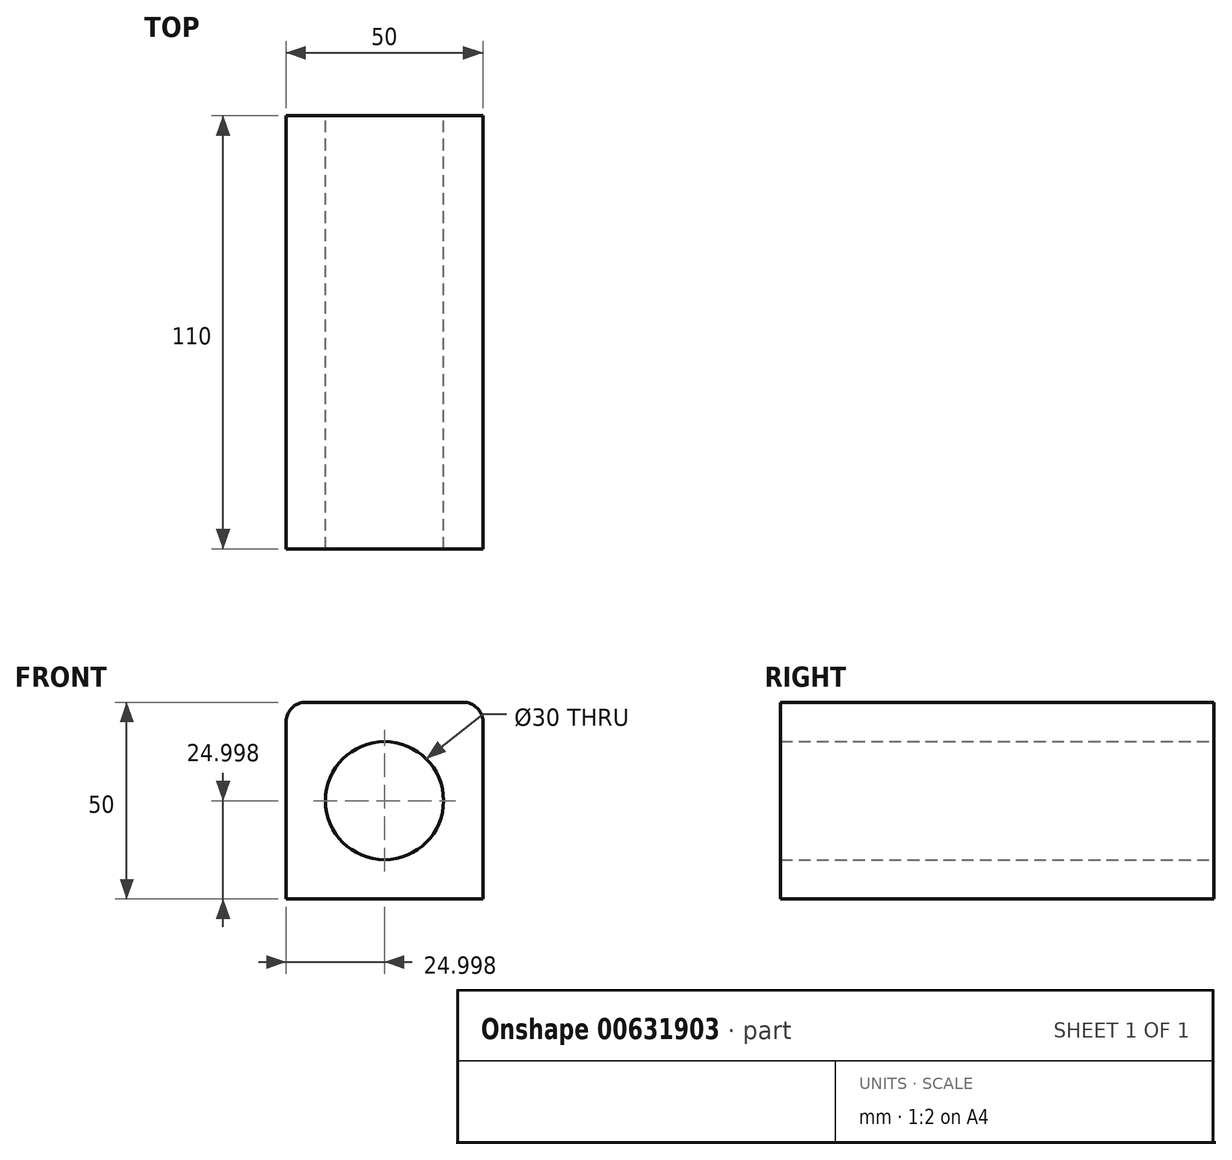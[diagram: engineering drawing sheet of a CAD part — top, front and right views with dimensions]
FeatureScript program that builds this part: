
annotation { "Feature Type Name" : "Feature", "Feature Type Description" : "" }
export const myFeature = defineFeature(function(context is Context, id is Id, definition is map)
    precondition{}
    {
        {
            var Q0;
            Q0=qCreatedBy(makeId("Front.planeOp"),FACE);
            var sketch = newSketch(context, id + "F0", { "sketchPlane" : qUnion([Q0])});
            skLineSegment(sketch, "E0.bottom", {"start": v(-42.08, 35.82) * mm, "end": v(7.92, 35.82) * mm});
            skLineSegment(sketch, "E0.top", {"start": v(-42.08, -14.18) * mm, "end": v(7.92, -14.18) * mm});
            skLineSegment(sketch, "E0.left", {"start": v(-42.08, 35.82) * mm, "end": v(-42.08, -14.18) * mm});
            skLineSegment(sketch, "E0.right", {"start": v(7.92, 35.82) * mm, "end": v(7.92, -14.18) * mm});
            skCircle(sketch, "E1", {"center": v(-17.08, 10.82) * mm, "radius": 15 * mm});
            skSolve(sketch);
        }
        {
            var Q0;
            Q0=makeQuery(id+"F0.imprint","IMPRINT",FACE,{"disambiguationData":[TD([[makeQuery(id+"F0.imprint","IMPRINT",EDGE,{"derivedFrom":sQuery(id+"F0.wireOp",EDGE,"E0.bottom")}),-1.0]])]});
            extrude(context, id + "F1", {"entities" : qUnion([Q0]), "depth" : 110 * mm, "offsetDistance" : 25 * mm});
        }
        {
            var Q0;
            Q0=makeQuery(id+"F1.opExtrude","SWEPT_EDGE",EDGE,{"disambiguationData":[OSD([sQuery(id+"F0.wireOp",EDGE,"E0.bottom"),sQuery(id+"F0.wireOp",EDGE,"E0.right")])]});
            var Q1;
            Q1=makeQuery(id+"F1.opExtrude","SWEPT_EDGE",EDGE,{"disambiguationData":[OSD([sQuery(id+"F0.wireOp",EDGE,"E0.bottom"),sQuery(id+"F0.wireOp",EDGE,"E0.left")])]});
            fillet(context, id + "F2", {"entities" : qUnion([Q0, Q1]), "radius" : 5 * mm, "tangentPropagation" : true, "allowEdgeOverflow" : false});
        }
    });
